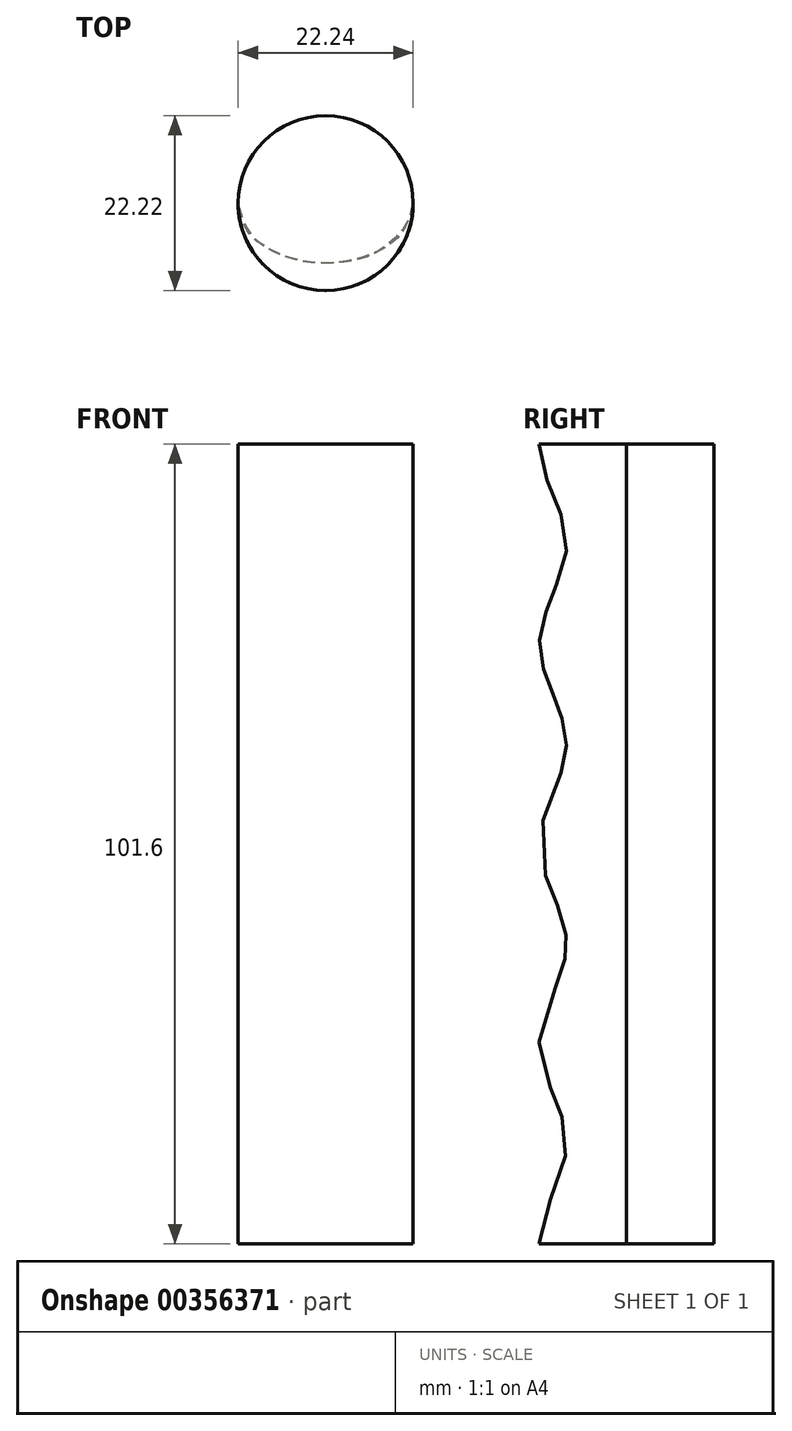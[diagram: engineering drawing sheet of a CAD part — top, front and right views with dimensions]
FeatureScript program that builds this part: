
annotation { "Feature Type Name" : "Feature", "Feature Type Description" : "" }
export const myFeature = defineFeature(function(context is Context, id is Id, definition is map)
    precondition{}
    {
        {
            var Q0;
            Q0=qCreatedBy(makeId("Top.planeOp"),FACE);
            var sketch = newSketch(context, id + "F0", { "sketchPlane" : qUnion([Q0])});
            skCircle(sketch, "E0", {"center": v(0, -25.4) * mm, "radius": 11.11 * mm});
            skSolve(sketch);
        }
        {
            var Q0;
            Q0=qCreatedBy(makeId("Top.planeOp"),FACE);
            cPlane(context, id + "F1", {"entities" : qUnion([Q0]), "cplaneType" : CPlaneType.OFFSET, "offset" : 101.6 * mm, "width" : 152.4 * mm, "height" : 152.4 * mm});
        }
        {
            var Q0;
            Q0=qCreatedBy(id+"F1.planeOp",FACE);
            var sketch = newSketch(context, id + "F2", { "sketchPlane" : qUnion([Q0])});
            skCircle(sketch, "E1", {"center": v(0, -25.4) * mm, "radius": 11.11 * mm});
            skSolve(sketch);
        }
        {
            var Q0;
            Q0=qCreatedBy(makeId("Top.planeOp"),FACE);
            cPlane(context, id + "F3", {"entities" : qUnion([Q0]), "cplaneType" : CPlaneType.OFFSET, "offset" : 25.4 * mm, "width" : 152.4 * mm, "height" : 152.4 * mm});
        }
        {
            var Q0;
            Q0=qCreatedBy(id+"F3.planeOp",FACE);
            cPlane(context, id + "F4", {"entities" : qUnion([Q0]), "cplaneType" : CPlaneType.OFFSET, "offset" : 25.4 * mm, "width" : 152.4 * mm, "height" : 152.4 * mm});
        }
        {
            var Q0;
            Q0=qCreatedBy(id+"F4.planeOp",FACE);
            cPlane(context, id + "F5", {"entities" : qUnion([Q0]), "cplaneType" : CPlaneType.OFFSET, "offset" : 25.4 * mm, "width" : 152.4 * mm, "height" : 152.4 * mm});
        }
        {
            var Q0;
            Q0=qCreatedBy(id+"F5.planeOp",FACE);
            var sketch = newSketch(context, id + "F6", { "sketchPlane" : qUnion([Q0])});
            skCircle(sketch, "E2", {"center": v(0, -25.4) * mm, "radius": 11.11 * mm});
            skSolve(sketch);
        }
        {
            var Q0;
            Q0=qCreatedBy(id+"F4.planeOp",FACE);
            var sketch = newSketch(context, id + "F7", { "sketchPlane" : qUnion([Q0])});
            skCircle(sketch, "E3", {"center": v(0, -25.4) * mm, "radius": 11.11 * mm});
            skSolve(sketch);
        }
        {
            var Q0;
            Q0=qCreatedBy(id+"F3.planeOp",FACE);
            var sketch = newSketch(context, id + "F8", { "sketchPlane" : qUnion([Q0])});
            skCircle(sketch, "E4", {"center": v(0, -25.4) * mm, "radius": 11.11 * mm});
            skSolve(sketch);
        }
        {
            var Q0;
            Q0=qCreatedBy(makeId("Top.planeOp"),FACE);
            cPlane(context, id + "F9", {"entities" : qUnion([Q0]), "cplaneType" : CPlaneType.OFFSET, "offset" : 12.7 * mm, "width" : 152.4 * mm, "height" : 152.4 * mm});
        }
        {
            var Q0;
            Q0=qCreatedBy(id+"F3.planeOp",FACE);
            cPlane(context, id + "F10", {"entities" : qUnion([Q0]), "cplaneType" : CPlaneType.OFFSET, "offset" : 12.7 * mm, "width" : 152.4 * mm, "height" : 152.4 * mm});
        }
        {
            var Q0;
            Q0=qCreatedBy(id+"F4.planeOp",FACE);
            cPlane(context, id + "F11", {"entities" : qUnion([Q0]), "cplaneType" : CPlaneType.OFFSET, "offset" : 12.7 * mm, "width" : 152.4 * mm, "height" : 152.4 * mm});
        }
        {
            var Q0;
            Q0=qCreatedBy(id+"F5.planeOp",FACE);
            cPlane(context, id + "F12", {"entities" : qUnion([Q0]), "cplaneType" : CPlaneType.OFFSET, "offset" : 12.7 * mm, "width" : 152.4 * mm, "height" : 152.4 * mm});
        }
        {
            var Q0;
            Q0=qCreatedBy(id+"F12.planeOp",FACE);
            var sketch = newSketch(context, id + "F13", { "sketchPlane" : qUnion([Q0])});
            skCircle(sketch, "E5", {"center": v(0, -25.4) * mm, "radius": 11.11 * mm});
            skPoint(sketch, "E6", {"position": v(-11.11, -25.4) * mm});
            skPoint(sketch, "E7", {"position": v(11.11, -25.4) * mm});
            skPoint(sketch, "E8", {"position": v(0, -14.29) * mm});
            skPoint(sketch, "E9", {"position": v(0, -33.02) * mm});
            skPoint(sketch, "E10", {"position": v(3.06, -32.78) * mm});
            skPoint(sketch, "E11", {"position": v(9.96, -28.52) * mm});
            skPoint(sketch, "E12", {"position": v(-3.06, -32.78) * mm});
            skPoint(sketch, "E13", {"position": v(-9.79, -29.19) * mm});
            skPoint(sketch, "E14", {"position": v(-6.28, -31.71) * mm});
            skPoint(sketch, "E15", {"position": v(6.33, -31.74) * mm});
            skFitSpline(sketch, "E16", {"points": [v(11.11, -25.4) * mm, v(9.96, -28.52) * mm, v(6.33, -31.74) * mm, v(3.06, -32.78) * mm, v(0, -33.02) * mm, v(-3.06, -32.78) * mm, v(-6.28, -31.71) * mm, v(-9.79, -29.19) * mm, v(-11.11, -25.4) * mm], "startDerivative": vector(0, -32.6) * mm, "endDerivative": vector(0, 29.69) * mm});
            skLineSegment(sketch, "E17", {"start": v(11.11, -25.4) * mm, "end": v(11.11, -31.36) * mm});
            skLineSegment(sketch, "E18", {"start": v(-11.11, -25.4) * mm, "end": v(-11.11, -31.64) * mm});
            skSolve(sketch);
        }
        {
            var Q0;
            Q0=qCreatedBy(id+"F11.planeOp",FACE);
            var sketch = newSketch(context, id + "F14", { "sketchPlane" : qUnion([Q0])});
            skCircle(sketch, "E19", {"center": v(0, -25.4) * mm, "radius": 11.11 * mm});
            skPoint(sketch, "E20", {"position": v(0, -33.02) * mm});
            skPoint(sketch, "E21", {"position": v(-11.11, -25.4) * mm});
            skPoint(sketch, "E22", {"position": v(-9.51, -29.34) * mm});
            skPoint(sketch, "E23", {"position": v(-6.28, -31.68) * mm});
            skPoint(sketch, "E24", {"position": v(-3.04, -32.73) * mm});
            skPoint(sketch, "E25", {"position": v(3.04, -32.73) * mm});
            skPoint(sketch, "E26", {"position": v(6.28, -31.68) * mm});
            skPoint(sketch, "E27", {"position": v(9.51, -29.34) * mm});
            skFitSpline(sketch, "E28", {"points": [v(-11.11, -25.4) * mm, v(-9.51, -29.34) * mm, v(-6.28, -31.68) * mm, v(-3.04, -32.73) * mm, v(0, -33.02) * mm, v(3.04, -32.73) * mm, v(6.28, -31.68) * mm, v(9.51, -29.34) * mm, v(11.11, -25.4) * mm], "startDerivative": vector(8.55, -31.72) * mm, "endDerivative": vector(8.55, 31.72) * mm});
            skSolve(sketch);
        }
        {
            var Q0;
            Q0=qCreatedBy(id+"F10.planeOp",FACE);
            var sketch = newSketch(context, id + "F15", { "sketchPlane" : qUnion([Q0])});
            skCircle(sketch, "E29", {"center": v(0, -25.4) * mm, "radius": 11.11 * mm});
            skPoint(sketch, "E30", {"position": v(-11.11, -25.4) * mm});
            skPoint(sketch, "E31", {"position": v(0, -33.02) * mm});
            skPoint(sketch, "E32", {"position": v(-9.51, -29.34) * mm});
            skPoint(sketch, "E33", {"position": v(-6.28, -31.68) * mm});
            skPoint(sketch, "E34", {"position": v(-3.04, -32.73) * mm});
            skPoint(sketch, "E35", {"position": v(6.28, -31.68) * mm});
            skPoint(sketch, "E36", {"position": v(3.04, -32.73) * mm});
            skPoint(sketch, "E37", {"position": v(9.51, -29.34) * mm});
            skPoint(sketch, "E38", {"position": v(11.11, -25.4) * mm});
            skFitSpline(sketch, "E39", {"points": [v(-11.11, -25.4) * mm, v(-9.51, -29.34) * mm, v(-6.28, -31.68) * mm, v(-3.04, -32.73) * mm, v(0, -33.02) * mm, v(3.04, -32.73) * mm, v(6.28, -31.68) * mm, v(9.51, -29.34) * mm, v(11.11, -25.4) * mm], "startDerivative": vector(8.55, -31.72) * mm, "endDerivative": vector(8.55, 31.72) * mm});
            skSolve(sketch);
        }
        {
            var Q0;
            Q0=qCreatedBy(id+"F9.planeOp",FACE);
            var sketch = newSketch(context, id + "F16", { "sketchPlane" : qUnion([Q0])});
            skCircle(sketch, "E40", {"center": v(0, -25.4) * mm, "radius": 11.11 * mm});
            skPoint(sketch, "E41", {"position": v(-11.11, -25.4) * mm});
            skFitSpline(sketch, "E42", {"points": [v(-11.11, -25.4) * mm, v(-9.51, -29.34) * mm, v(-6.28, -31.68) * mm, v(-3.04, -32.73) * mm, v(0, -33.02) * mm, v(3.04, -32.73) * mm, v(6.28, -31.68) * mm, v(9.51, -29.34) * mm, v(11.11, -25.4) * mm], "startDerivative": vector(8.55, -31.72) * mm, "endDerivative": vector(8.55, 31.72) * mm});
            skSolve(sketch);
        }
        {
            var Q0;
            Q0=makeQuery(id+"F2.imprint","IMPRINT",FACE,{"disambiguationData":[TD([[makeQuery(id+"F2.imprint","IMPRINT",EDGE,{"derivedFrom":sQuery(id+"F2.wireOp",EDGE,"E1")}),1.0]])]});
            var Q1;
            {var subQ0=sQuery(id+"F13.wireOp",EDGE,"E16");Q1=makeQuery(id+"F13.imprint","IMPRINT",FACE,{"disambiguationData":[TD([[makeQuery(id+"F13.imprint","IMPRINT",EDGE,{"derivedFrom":subQ0}),-1.0]])]});}
            var Q2;
            Q2=makeQuery(id+"F6.imprint","IMPRINT",FACE,{"disambiguationData":[TD([[makeQuery(id+"F6.imprint","IMPRINT",EDGE,{"derivedFrom":sQuery(id+"F6.wireOp",EDGE,"E2")}),1.0]])]});
            var Q3;
            {var subQ0=sQuery(id+"F14.wireOp",EDGE,"E28");Q3=makeQuery(id+"F14.imprint","IMPRINT",FACE,{"disambiguationData":[TD([[makeQuery(id+"F14.imprint","IMPRINT",EDGE,{"derivedFrom":subQ0}),1.0]])]});}
            var Q4;
            Q4=makeQuery(id+"F7.imprint","IMPRINT",FACE,{"disambiguationData":[TD([[makeQuery(id+"F7.imprint","IMPRINT",EDGE,{"derivedFrom":sQuery(id+"F7.wireOp",EDGE,"E3")}),1.0]])]});
            var Q5;
            {var subQ0=sQuery(id+"F15.wireOp",EDGE,"E39");Q5=makeQuery(id+"F15.imprint","IMPRINT",FACE,{"disambiguationData":[TD([[makeQuery(id+"F15.imprint","IMPRINT",EDGE,{"derivedFrom":subQ0}),1.0]])]});}
            var Q6;
            Q6=makeQuery(id+"F8.imprint","IMPRINT",FACE,{"disambiguationData":[TD([[makeQuery(id+"F8.imprint","IMPRINT",EDGE,{"derivedFrom":sQuery(id+"F8.wireOp",EDGE,"E4")}),1.0]])]});
            var Q7;
            {var subQ0=sQuery(id+"F16.wireOp",EDGE,"E42");Q7=makeQuery(id+"F16.imprint","IMPRINT",FACE,{"disambiguationData":[TD([[makeQuery(id+"F16.imprint","IMPRINT",EDGE,{"derivedFrom":subQ0}),1.0]])]});}
            var Q8;
            Q8=makeQuery(id+"F0.imprint","IMPRINT",FACE,{"disambiguationData":[TD([[makeQuery(id+"F0.imprint","IMPRINT",EDGE,{"derivedFrom":sQuery(id+"F0.wireOp",EDGE,"E0")}),1.0]])]});
            loft(context, id + "F17", {"sheetProfilesArray" : [{ "sheetProfileEntities" : qUnion([Q0]) }, { "sheetProfileEntities" : qUnion([Q1]) }, { "sheetProfileEntities" : qUnion([Q2]) }, { "sheetProfileEntities" : qUnion([Q3]) }, { "sheetProfileEntities" : qUnion([Q4]) }, { "sheetProfileEntities" : qUnion([Q5]) }, { "sheetProfileEntities" : qUnion([Q6]) }, { "sheetProfileEntities" : qUnion([Q7]) }, { "sheetProfileEntities" : qUnion([Q8]) }], "startCondition" : LoftEndDerivativeType.NORMAL_TO_PROFILE, "startMagnitude" : 1, "endCondition" : LoftEndDerivativeType.NORMAL_TO_PROFILE, "endMagnitude" : 1});
        }
    });
